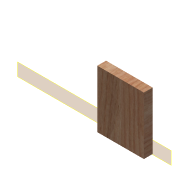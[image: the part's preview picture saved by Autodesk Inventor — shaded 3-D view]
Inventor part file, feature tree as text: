
AUTODESK INVENTOR PART (.ipt)
format: ipt  version: 2015 (Build 190159000, 159)  size: 82,944 bytes
history: native  units: in
note: dims shown in document units (in); Inventor stores cm internally (conversion verified against a paired STEP export)
features: reference x4, plane x1, extrude x1, sketch x1
ambient origin geometry x8: Origin, YZ Plane, XZ Plane, XY Plane, X Axis, Y Axis, Z Axis, Center Point
bodies: Solid1 (feature_tree)
feature tree (7):
  plane  "Work Plane1"
  extrude  "Extrusion1"  Depth=0.75in TaperAngle=0.0deg
  sketch  "Sketch1"  dims[d0=4.0in d1=0.75in d2=0.0in]
  reference  "Reference1"
  reference  "Reference2"
  reference  "Reference3"
  reference  "Reference4"
